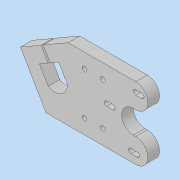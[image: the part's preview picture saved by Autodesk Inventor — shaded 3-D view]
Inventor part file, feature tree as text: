
AUTODESK INVENTOR PART (.ipt)
format: ipt  version: 2017 (Build 210142000, 142)  size: 204,288 bytes
history: native  units: in
note: dims shown in document units (in); Inventor stores cm internally (conversion verified against a paired STEP export)
features: sketch x3, extrude x3, fillet x2, plane x1
ambient origin geometry x8: Origin, YZ Plane, XZ Plane, XY Plane, X Axis, Y Axis, Z Axis, Center Point
bodies: Solid8 (feature_tree)
feature tree (9):
  sketch  "sketch_plate"  dims[d8=0.72in d9=0.56in]
  extrude  "Extrusion10"  Depth=0.72in
  sketch  "sketch_clampscrew"  dims[d10=0.41in d13=0.45in]
  extrude  "extr_clampscrew"  Depth=0.45in
  plane  "Work Plane1"
  sketch  "sketch_clampscrewhead"  dims[d14=0.45in d15=0.0787in d17=2.3228in d18=0.313in d19=0.36in d20=0.365in d21=30.0deg d22=0.3287in d23=2.5606in d25=0.159in d26=0.159in d27=0.159in d28=0.159in d32=0.75in d33=0.1575in d34=0.1575in d35=0.1575in d36=0.1575in d38=1.2205in d39=1.2205in d40=1.2205in d41=1.2205in d42=0.5906in d43=1.378in d44=1.378in d49=0.1575in d50=0.1575in d51=0.1575in d52=0.1575in d53=0.1969in d54=2.3228in d55=2.6406in d56=0.75in d57=0.1969in d58=0.1969in d59=0.1969in d60=0.1575in d61=0.1575in d62=0.1575in d63=0.1575in d68=0.0344in d69=0.0344in d70=1.2205in d71=1.2205in d72=1.2205in d73=1.2205in d87=0.159in d88=0.5in d89=0.0in d90=0.5in d91=0.0in d92=2.1864in d93=0.1575in d94=0.1575in d95=0.9843in d96=0.375in d97=0.0in]
  extrude  "extr_clampscrewhead"  Depth=0.0787in
  fillet  "Fillet1"  Radius=2.3228in
  fillet  "Fillet2"  Radius=0.313in
